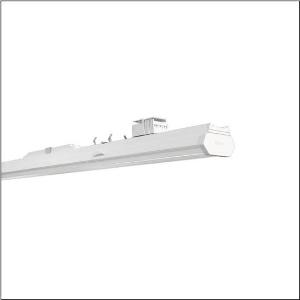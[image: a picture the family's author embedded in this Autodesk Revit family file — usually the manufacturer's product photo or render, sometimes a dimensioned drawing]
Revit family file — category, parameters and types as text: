
# Revit family: licross_r__21_protected_ho_52td12dn4axm_e376
name_source: partatom
category: Lighting Fixtures
units: mm (PartAtom-declared; Revit-internal decimal feet)

## family parameters
Cut with Voids When Loaded = No
Host = Face
Light Source = No
Part Type = Normal
Room Calculation Point = No
Round Connector Dimension = Use Diameter
Shared = No

## types (1)
- --- (1 x LED, 10000 lm, 56 W, 4000K)
    Apparent Load = 56 VA
    CIE Flux Codes = 70 91 97 98 100
    Color Rendering = 80
    Color Temperature = 4000K
    Default Elevation = 1800 mm
    Description = Licross® 21 Protected HO, luminaire insert, of sheet steel, galvanised, coil coated, white, length: 1.500mm, width: 90mm, height: 103mm, LED rated luminous flux: 10.000lm, light colour: 840, control gear: DALI 2, with plug, 5-pole, with phase selection, mains connection: 220..240V, AC, 50/60Hz, rated input power: 56W, halogen-free wiring, primary light control with lens, of plastic, primary optical cover: cover, of PMMA, light emission: direct distribution, primary light characteristic: symmetric, protection rating (complete): IP54, insulation class (complete): insulation class I (protective earthing), certification: CE, ENEC, VDE, UKCA, protection symbol: D if used in an environment with non-conductive dust loads with corresponding accessories, impact resistance: IK06, permissible ambient temperature for indoor applications: -25..+45°C, corresponds to IFS (International Featured Standards) requirements for safety and quality in the food industry, reducing of maximum allowable ambient temperature of 5°C with ceiling mounting, LABS conformity tested according to VDMA 24364:2018-05, packaging unit: 1 piece
    Height = 92 mm
    Lamp = 1 x LED
    Lamp Light Flux = 10000 lm
    Lamp Power = 56 W
    Lamp count = 1
    Length = 1500 mm
    Luminous efficacy = 179 lm/W
    Manufacturer = Siteco
    ModVariant = No
    Model = 52TD12DN4AXM
    Mounting Place = Ceiling
    Mounting Type = Pendant
    Number of Poles = 1
    OnlyDefault = Yes
    Power Factor = 1
    Product Name = Licross® 21 Protected HO
    Product group = luminaire insert
    ProductGroupID = 901
    Protection Class = Protection class I
    Protection Degree = IP 54
    RLX_Detail_Level = 1
    RLX_Emergency_Light_Flux = 0 lm
    RLX_Emergency_Type = 0
    RLX_Emergency_Type_DB = No
    RlxData = <blob elided: 24237 chars, md5=202980aa>
    Socket = socket
    Standby Power = 0 W
    System Light Flux = 10000 lm
    System Power = 56 W
    Type Comments = factory setting: luminous flux: 100 % | dim-lin: 254 | 321 mA
    Type Image = l_1256148.jpg
    URL = http://relux.com
    VarID = @adj_060581
    Voltage = 0 V
    Weight = 0.00 kg
    Width = 88 mm

## geometry (parser evidence)
native form markers: Blend x4, Sweep x10
no freeform markers — native parametric forms only
